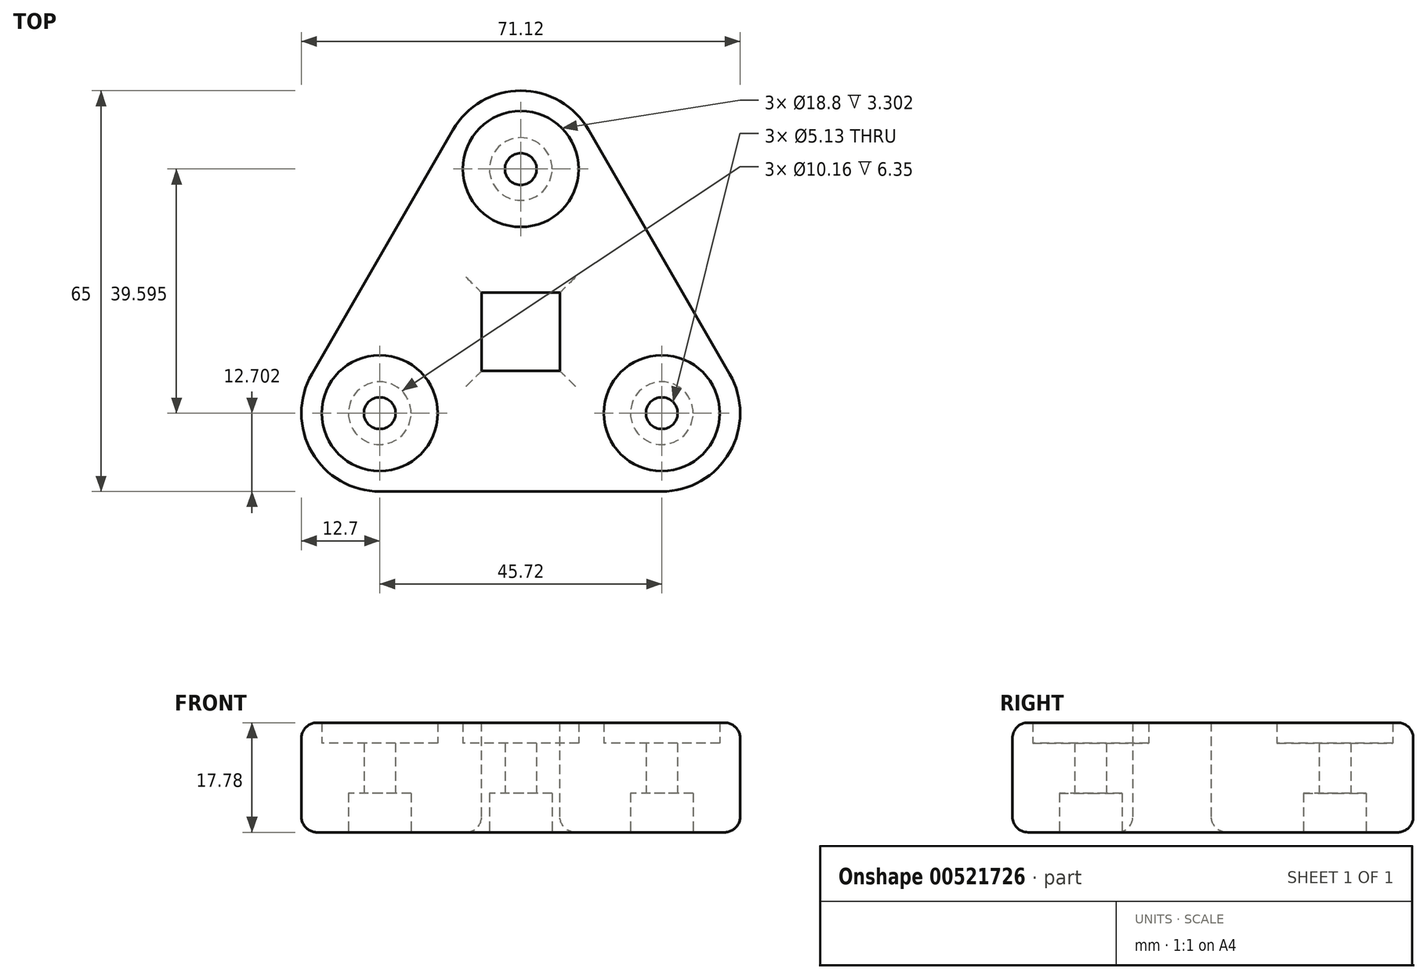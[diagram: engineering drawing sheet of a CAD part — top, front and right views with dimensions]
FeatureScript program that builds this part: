
annotation { "Feature Type Name" : "Feature", "Feature Type Description" : "" }
export const myFeature = defineFeature(function(context is Context, id is Id, definition is map)
    precondition{}
    {
        {
            var Q0;
            Q0=qCreatedBy(makeId("Top.planeOp"),FACE);
            var sketch = newSketch(context, id + "F0", { "sketchPlane" : qUnion([Q0])});
            skLineSegment(sketch, "E0", {"start": v(0, 26.4) * mm, "end": v(22.86, -13.2) * mm, "construction": true});
            skLineSegment(sketch, "E1", {"start": v(22.86, -13.2) * mm, "end": v(-22.86, -13.2) * mm, "construction": true});
            skLineSegment(sketch, "E2", {"start": v(-22.86, -13.2) * mm, "end": v(0, 26.4) * mm, "construction": true});
            skCircle(sketch, "E3", {"center": v(0, 0) * mm, "radius": 13.2 * mm, "construction": true});
            skCircle(sketch, "E4", {"center": v(0, 26.4) * mm, "radius": 9.4 * mm});
            skCircle(sketch, "E5", {"center": v(22.86, -13.2) * mm, "radius": 9.4 * mm});
            skCircle(sketch, "E6", {"center": v(-22.86, -13.2) * mm, "radius": 9.4 * mm});
            skLineSegment(sketch, "E7", {"start": v(-11, 32.75) * mm, "end": v(-33.86, -6.85) * mm});
            skLineSegment(sketch, "E8", {"start": v(-22.86, -25.9) * mm, "end": v(22.86, -25.9) * mm});
            skLineSegment(sketch, "E9", {"start": v(33.86, -6.85) * mm, "end": v(11, 32.75) * mm});
            skArc(sketch, "E10", {"start": v(22.86, -25.9) * mm, "mid": v(33.86, -19.55) * mm, "end": v(33.86, -6.85) * mm});
            skArc(sketch, "E11.trimOffspring", {"start": v(11, 32.75) * mm, "mid": v(0, 39.1) * mm, "end": v(-11, 32.75) * mm});
            skArc(sketch, "E12.trimOffspring", {"start": v(-33.86, -6.85) * mm, "mid": v(-33.86, -19.55) * mm, "end": v(-22.86, -25.9) * mm});
            skSolve(sketch);
        }
        {
            var Q0;
            Q0=makeQuery(id+"F0.imprint","IMPRINT",FACE,{"disambiguationData":[TD([[makeQuery(id+"F0.imprint","IMPRINT",EDGE,{"derivedFrom":sQuery(id+"F0.wireOp",EDGE,"E4")}),-1.0]])]});
            var sketch = newSketch(context, id + "F1", { "sketchPlane" : qUnion([Q0])});
            skLineSegment(sketch, "E13.bottom", {"start": v(6.35, 6.35) * mm, "end": v(-6.35, 6.35) * mm});
            skLineSegment(sketch, "E13.top", {"start": v(6.35, -6.35) * mm, "end": v(-6.35, -6.35) * mm});
            skLineSegment(sketch, "E13.left", {"start": v(6.35, 6.35) * mm, "end": v(6.35, -6.35) * mm});
            skLineSegment(sketch, "E13.right", {"start": v(-6.35, 6.35) * mm, "end": v(-6.35, -6.35) * mm});
            skPoint(sketch, "E13.middle", {"position": v(0, 0) * mm});
            skSolve(sketch);
        }
        {
            var Q0;
            Q0=makeQuery(id+"F0.imprint","IMPRINT",FACE,{"disambiguationData":[TD([[makeQuery(id+"F0.imprint","IMPRINT",EDGE,{"derivedFrom":sQuery(id+"F0.wireOp",EDGE,"E4")}),-1.0]])]});
            extrude(context, id + "F2", {"entities" : qUnion([Q0]), "depth" : 17.78 * mm, "offsetDistance" : 25.4 * mm});
        }
        {
            var Q0;
            Q0=makeQuery(id+"F0.imprint","IMPRINT",FACE,{"disambiguationData":[TD([[makeQuery(id+"F0.imprint","IMPRINT",EDGE,{"derivedFrom":sQuery(id+"F0.wireOp",EDGE,"E6")}),1.0]])]});
            var Q1;
            Q1=makeQuery(id+"F0.imprint","IMPRINT",FACE,{"disambiguationData":[TD([[makeQuery(id+"F0.imprint","IMPRINT",EDGE,{"derivedFrom":sQuery(id+"F0.wireOp",EDGE,"E5")}),1.0]])]});
            var Q2;
            Q2=makeQuery(id+"F0.imprint","IMPRINT",FACE,{"disambiguationData":[TD([[makeQuery(id+"F0.imprint","IMPRINT",EDGE,{"derivedFrom":sQuery(id+"F0.wireOp",EDGE,"E4")}),1.0]])]});
            extrude(context, id + "F3", {"entities" : qUnion([Q0, Q1, Q2]), "operationType" : NewBodyOperationType.ADD, "depth" : 14.48 * mm, "offsetDistance" : 25.4 * mm});
        }
        {
            var Q0;
            Q0=makeQuery(id+"F1.imprint","IMPRINT",FACE,{"disambiguationData":[TD([[makeQuery(id+"F1.imprint","IMPRINT",EDGE,{"derivedFrom":sQuery(id+"F1.wireOp",EDGE,"E13.bottom")}),1.0]])]});
            extrude(context, id + "F4", {"entities" : qUnion([Q0]), "operationType" : NewBodyOperationType.REMOVE, "endBound" : BoundingType.THROUGH_ALL, "oppositeDirection" : true, "depth" : 25.4 * mm, "offsetDistance" : 25.4 * mm, "hasSecondDirection" : true, "secondDirectionBound" : SecondDirectionBoundingType.THROUGH_ALL, "secondDirectionOppositeDirection" : false, "secondDirectionDepth" : 12.38 * mm});
        }
        {
            var Q0;
            Q0=sQuery(id+"F0.wireOp",VERTEX,"E6.center");
            var Q1;
            Q1=sQuery(id+"F0.wireOp",VERTEX,"E5.center");
            var Q2;
            Q2=sQuery(id+"F0.wireOp",VERTEX,"E0.start");
            var Q3;
            Q3=makeQuery(id+"F2.opExtrude","SWEPT_BODY",BODY,{"disambiguationData":[OSD([sQuery(id+"F0.wireOp",EDGE,"E4"),sQuery(id+"F0.wireOp",EDGE,"E5"),sQuery(id+"F0.wireOp",EDGE,"E6"),sQuery(id+"F0.wireOp",EDGE,"E7"),sQuery(id+"F0.wireOp",EDGE,"E8"),sQuery(id+"F0.wireOp",EDGE,"E9"),sQuery(id+"F0.wireOp",EDGE,"E10"),sQuery(id+"F0.wireOp",EDGE,"E11.trimOffspring"),sQuery(id+"F0.wireOp",EDGE,"E12.trimOffspring")])]});
            hole(context, id + "F5", {"style" : HoleStyle.SIMPLE, "endStyle" : HoleEndStyle.THROUGH, "oppositeDirection" : true, "holeDiameter" : 5.13 * mm, "isTappedThrough" : true, "tappedDepth" : 12.7 * mm, "tapClearance" : 3, "locations" : qUnion([Q0, Q1, Q2]), "scope" : qUnion([Q3])});
        }
        {
            var Q0;
            Q0=makeQuery(id+"F2.opExtrude","CAP_EDGE",EDGE,{"disambiguationData":[OSD([sQuery(id+"F0.wireOp",EDGE,"E7")])],"isStart":false});
            fillet(context, id + "F6", {"entities" : qUnion([Q0]), "radius" : 2.54 * mm, "tangentPropagation" : true, "allowEdgeOverflow" : false});
        }
        {
            var Q0;
            Q0=makeQuery(id+"F2.opExtrude","CAP_EDGE",EDGE,{"disambiguationData":[OSD([sQuery(id+"F0.wireOp",EDGE,"E9")])],"isStart":true});
            fillet(context, id + "F7", {"entities" : qUnion([Q0]), "radius" : 2.54 * mm, "tangentPropagation" : true, "allowEdgeOverflow" : false});
        }
        {
            var Q0;
            {var subQ0=sQuery(id+"F0.wireOp",EDGE,"E6");var subQ1=sQuery(id+"F0.wireOp",EDGE,"E5");var subQ2=sQuery(id+"F0.wireOp",EDGE,"E4");Q0=makeQuery(id+"F4.boolean.opBoolean","INTERSECT",EDGE,{"derivedFrom":[makeQuery(id+"F3Cv4s5UGB3mtFy_1.boolean.opBoolean","MERGE",FACE,{"derivedFrom":[makeQuery(id+"Fjo01PQs2WGaySU_1.boolean.opBoolean","MERGE",FACE,{"derivedFrom":[makeQuery(id+"F2.opExtrude","CAP_FACE",FACE,{"disambiguationData":[OSD([subQ2,subQ1,subQ0,sQuery(id+"F0.wireOp",EDGE,"E7"),sQuery(id+"F0.wireOp",EDGE,"E8"),sQuery(id+"F0.wireOp",EDGE,"E9"),sQuery(id+"F0.wireOp",EDGE,"E10"),sQuery(id+"F0.wireOp",EDGE,"E11.trimOffspring"),sQuery(id+"F0.wireOp",EDGE,"E12.trimOffspring")])],"isStart":true}),makeQuery(id+"Fjo01PQs2WGaySU_1.opExtrude","CAP_FACE",FACE,{"disambiguationData":[OSD([subQ2])],"isStart":true}),makeQuery(id+"Fjo01PQs2WGaySU_1.opExtrude","CAP_FACE",FACE,{"disambiguationData":[OSD([subQ1])],"isStart":true})]}),makeQuery(id+"F3Cv4s5UGB3mtFy_1.opExtrude","CAP_FACE",FACE,{"disambiguationData":[OSD([subQ0])],"isStart":true})]}),makeQuery(id+"F4.opExtrude","SWEPT_FACE",FACE,{"disambiguationData":[OSD([sQuery(id+"F1.wireOp",EDGE,"E13.left")])]})]});}
            var Q1;
            {var subQ0=sQuery(id+"F0.wireOp",EDGE,"E6");var subQ1=sQuery(id+"F0.wireOp",EDGE,"E5");var subQ2=sQuery(id+"F0.wireOp",EDGE,"E4");Q1=makeQuery(id+"F4.boolean.opBoolean","INTERSECT",EDGE,{"derivedFrom":[makeQuery(id+"F3Cv4s5UGB3mtFy_1.boolean.opBoolean","MERGE",FACE,{"derivedFrom":[makeQuery(id+"Fjo01PQs2WGaySU_1.boolean.opBoolean","MERGE",FACE,{"derivedFrom":[makeQuery(id+"F2.opExtrude","CAP_FACE",FACE,{"disambiguationData":[OSD([subQ2,subQ1,subQ0,sQuery(id+"F0.wireOp",EDGE,"E7"),sQuery(id+"F0.wireOp",EDGE,"E8"),sQuery(id+"F0.wireOp",EDGE,"E9"),sQuery(id+"F0.wireOp",EDGE,"E10"),sQuery(id+"F0.wireOp",EDGE,"E11.trimOffspring"),sQuery(id+"F0.wireOp",EDGE,"E12.trimOffspring")])],"isStart":true}),makeQuery(id+"Fjo01PQs2WGaySU_1.opExtrude","CAP_FACE",FACE,{"disambiguationData":[OSD([subQ2])],"isStart":true}),makeQuery(id+"Fjo01PQs2WGaySU_1.opExtrude","CAP_FACE",FACE,{"disambiguationData":[OSD([subQ1])],"isStart":true})]}),makeQuery(id+"F3Cv4s5UGB3mtFy_1.opExtrude","CAP_FACE",FACE,{"disambiguationData":[OSD([subQ0])],"isStart":true})]}),makeQuery(id+"F4.opExtrude","SWEPT_FACE",FACE,{"disambiguationData":[OSD([sQuery(id+"F1.wireOp",EDGE,"E13.bottom")])]})]});}
            var Q2;
            {var subQ0=sQuery(id+"F0.wireOp",EDGE,"E6");var subQ1=sQuery(id+"F0.wireOp",EDGE,"E5");var subQ2=sQuery(id+"F0.wireOp",EDGE,"E4");Q2=makeQuery(id+"F4.boolean.opBoolean","INTERSECT",EDGE,{"derivedFrom":[makeQuery(id+"F3Cv4s5UGB3mtFy_1.boolean.opBoolean","MERGE",FACE,{"derivedFrom":[makeQuery(id+"Fjo01PQs2WGaySU_1.boolean.opBoolean","MERGE",FACE,{"derivedFrom":[makeQuery(id+"F2.opExtrude","CAP_FACE",FACE,{"disambiguationData":[OSD([subQ2,subQ1,subQ0,sQuery(id+"F0.wireOp",EDGE,"E7"),sQuery(id+"F0.wireOp",EDGE,"E8"),sQuery(id+"F0.wireOp",EDGE,"E9"),sQuery(id+"F0.wireOp",EDGE,"E10"),sQuery(id+"F0.wireOp",EDGE,"E11.trimOffspring"),sQuery(id+"F0.wireOp",EDGE,"E12.trimOffspring")])],"isStart":true}),makeQuery(id+"Fjo01PQs2WGaySU_1.opExtrude","CAP_FACE",FACE,{"disambiguationData":[OSD([subQ2])],"isStart":true}),makeQuery(id+"Fjo01PQs2WGaySU_1.opExtrude","CAP_FACE",FACE,{"disambiguationData":[OSD([subQ1])],"isStart":true})]}),makeQuery(id+"F3Cv4s5UGB3mtFy_1.opExtrude","CAP_FACE",FACE,{"disambiguationData":[OSD([subQ0])],"isStart":true})]}),makeQuery(id+"F4.opExtrude","SWEPT_FACE",FACE,{"disambiguationData":[OSD([sQuery(id+"F1.wireOp",EDGE,"E13.right")])]})]});}
            var Q3;
            {var subQ0=sQuery(id+"F0.wireOp",EDGE,"E6");var subQ1=sQuery(id+"F0.wireOp",EDGE,"E5");var subQ2=sQuery(id+"F0.wireOp",EDGE,"E4");Q3=makeQuery(id+"F4.boolean.opBoolean","INTERSECT",EDGE,{"derivedFrom":[makeQuery(id+"F3Cv4s5UGB3mtFy_1.boolean.opBoolean","MERGE",FACE,{"derivedFrom":[makeQuery(id+"Fjo01PQs2WGaySU_1.boolean.opBoolean","MERGE",FACE,{"derivedFrom":[makeQuery(id+"F2.opExtrude","CAP_FACE",FACE,{"disambiguationData":[OSD([subQ2,subQ1,subQ0,sQuery(id+"F0.wireOp",EDGE,"E7"),sQuery(id+"F0.wireOp",EDGE,"E8"),sQuery(id+"F0.wireOp",EDGE,"E9"),sQuery(id+"F0.wireOp",EDGE,"E10"),sQuery(id+"F0.wireOp",EDGE,"E11.trimOffspring"),sQuery(id+"F0.wireOp",EDGE,"E12.trimOffspring")])],"isStart":true}),makeQuery(id+"Fjo01PQs2WGaySU_1.opExtrude","CAP_FACE",FACE,{"disambiguationData":[OSD([subQ2])],"isStart":true}),makeQuery(id+"Fjo01PQs2WGaySU_1.opExtrude","CAP_FACE",FACE,{"disambiguationData":[OSD([subQ1])],"isStart":true})]}),makeQuery(id+"F3Cv4s5UGB3mtFy_1.opExtrude","CAP_FACE",FACE,{"disambiguationData":[OSD([subQ0])],"isStart":true})]}),makeQuery(id+"F4.opExtrude","SWEPT_FACE",FACE,{"disambiguationData":[OSD([sQuery(id+"F1.wireOp",EDGE,"E13.top")])]})]});}
            fillet(context, id + "F8", {"entities" : qUnion([Q0, Q1, Q2, Q3]), "radius" : 2.54 * mm, "tangentPropagation" : true, "allowEdgeOverflow" : false});
        }
        {
            var Q0;
            Q0=makeQuery(id+"F1.imprint","IMPRINT",FACE,{"disambiguationData":[TD([[makeQuery(id+"F1.imprint","IMPRINT",EDGE,{"derivedFrom":sQuery(id+"F1.wireOp",EDGE,"E13.bottom")}),-1.0]])]});
            var sketch = newSketch(context, id + "F9", { "sketchPlane" : qUnion([Q0])});
            skCircle(sketch, "E14", {"center": v(22.86, -13.2) * mm, "radius": 5.08 * mm});
            skPoint(sketch, "E15", {"position": v(0, 0) * mm});
            skCircle(sketch, "E16.1.0", {"center": v(0, 26.4) * mm, "radius": 5.08 * mm});
            skCircle(sketch, "E16.2.0", {"center": v(-22.86, -13.2) * mm, "radius": 5.08 * mm});
            skSolve(sketch);
        }
        {
            var Q0;
            Q0 = qSketchRegion(id + "F9", true);
            extrude(context, id + "F10", {"entities" : qUnion([Q0]), "operationType" : NewBodyOperationType.REMOVE, "depth" : 6.35 * mm, "offsetDistance" : 25.4 * mm});
        }
    });
